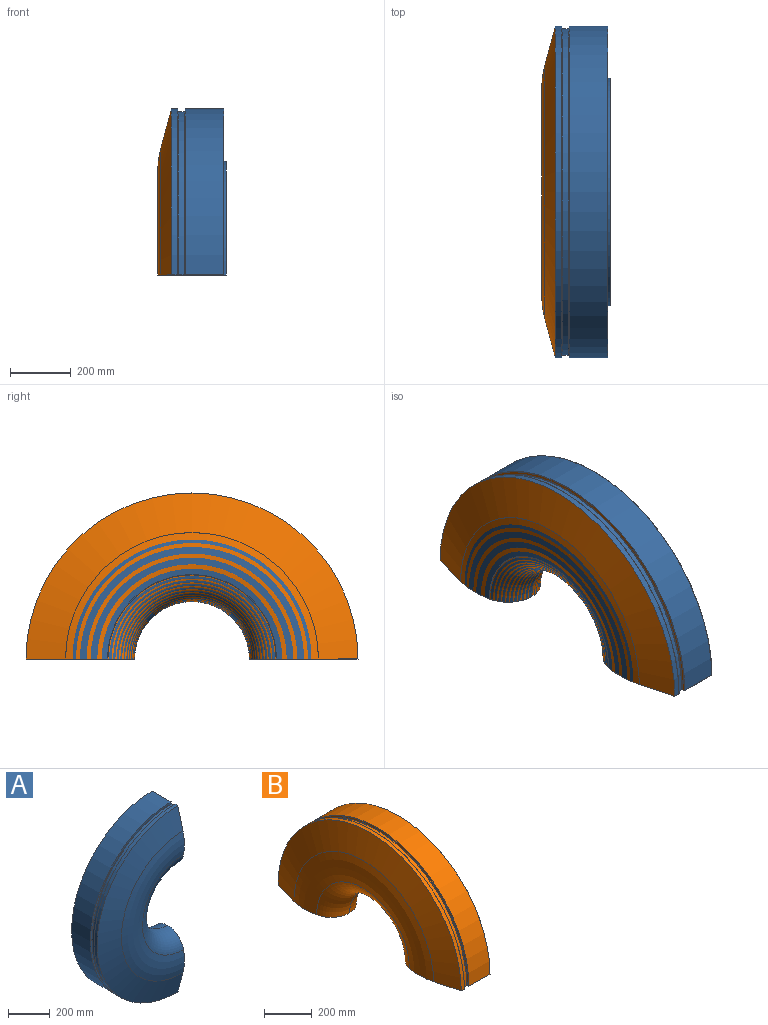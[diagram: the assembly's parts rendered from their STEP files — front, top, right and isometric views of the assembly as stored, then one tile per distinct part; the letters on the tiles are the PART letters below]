
ASSEMBLY  parts=2 mates=1
PART A: 24 faces, bbox 595.3x225x1190.6 mm
  f0: plane 356.3x225mm, normal (1,0,0), area 68121mm2, adj f1,f2,f3,f4,f5,f6,f7,f8
  f1: cone r=414.61mm half-angle=75deg, axis (0,1,0), area 202583mm2, adj f0,f2,f22,f23
  f2: cylinder r=544.5mm len=1089mm, axis (0,-1,0), area 34211.9mm2, adj f0,f1,f3,f23
  f3: plane 1089x544.5mm, normal (0,1,0), area 16948.9mm2, adj f0,f2,f4,f23
  f4: torus R=534.5mm, axis (0,-1,0), area 2634.5mm2, adj f0,f3,f5,f23
  f5: cylinder r=533.5mm len=1067mm, axis (0,-1,0), area 838mm2, adj f0,f4,f6,f23
  f6: cone r=533.5mm half-angle=45deg, axis (0,1,0), area 3560.4mm2, adj f0,f5,f7,f23
  f7: cylinder r=535mm len=1070mm, axis (0,-1,0), area 31934.3mm2, adj f0,f6,f8,f23
  f8: cone r=535mm half-angle=45deg, axis (0,-1,0), area 3560.4mm2, adj f0,f7,f9,f23
  f9: cylinder r=533.5mm len=1067mm, axis (0,-1,0), area 838mm2, adj f0,f8,f10,f23
  f10: torus R=534.5mm, axis (0,-1,0), area 2634.5mm2, adj f0,f9,f11,f23
  f11: plane 1089x544.5mm, normal (0,-1,0), area 16948.9mm2, adj f0,f10,f12,f23
  f12: cylinder r=544.5mm len=1089mm, axis (0,-1,0), area 217245.8mm2, adj f0,f11,f13,f23
  f13: plane 1089x544.5mm, normal (0,1,0), area 235892.8mm2, adj f0,f12,f14,f23
  f14: torus R=381.5mm, axis (0,-1,0), area 1885.8mm2, adj f0,f13,f15,f23
  f15: plane 763x381.5mm, normal (0,1,0), area 9487.6mm2, adj f0,f14,f16,f23
  f16: torus R=373.5mm, axis (0,-1,0), area 1840mm2, adj f0,f15,f17,f23
  f17: cylinder r=372.5mm len=745mm, axis (0,-1,0), area 9361.9mm2, adj f0,f16,f18,f23
  f18: plane 745x372.5mm, normal (0,1,0), area 41217.7mm2, adj f0,f17,f19,f23
  f19: torus R=404.55mm, axis (0,-1,0), area 72929.8mm2, adj f0,f18,f20,f23
  f20: torus R=286.2mm, axis (0,-1,0), area 84815.3mm2, adj f0,f19,f21,f23
  f21: torus R=298.2mm, axis (0,-1,0), area 104462.4mm2, adj f0,f20,f22,f23
  f22: torus R=337mm, axis (0,-1,0), area 151103.6mm2, adj f0,f1,f21,f23
  f23: plane 356.3x225mm, normal (1,0,0), area 68121mm2, adj f1,f2,f3,f4,f5,f6,f7,f8
PART B: 24 faces, bbox 225x1191.2x595.6 mm
  f0: plane 763x381.5mm, normal (1,0,0), area 9487.6mm2, adj f17,f18,f19,f20
  f1: plane 1087x543.5mm, normal (1,0,0), area 234183.7mm2, adj f17,f18,f19,f21
  f2: cylinder r=544.5mm len=1089mm, axis (-1,0,0), area 213824.6mm2, adj f17,f18,f21,f22
  f3: plane 1087x543.5mm, normal (-1,0,0), area 14399.9mm2, adj f4,f17,f18,f22
  f4: torus R=535mm, axis (-1,0,0), area 7906.2mm2, adj f3,f5,f17,f18
  f5: cylinder r=535mm len=1070mm, axis (-1,0,0), area 31934.3mm2, adj f4,f6,f17,f18
  f6: torus R=535mm, axis (-1,0,0), area 7906.2mm2, adj f5,f7,f17,f18
  f7: plane 1087x543.5mm, normal (1,0,0), area 14399.9mm2, adj f6,f17,f18,f23
  f8: cylinder r=544.5mm len=1089mm, axis (-1,0,0), area 32501.3mm2, adj f9,f17,f18,f23
  f9: cone r=544.5mm half-angle=75deg, axis (1,0,0), area 202400.5mm2, adj f8,f10,f17,f18
  f10: torus R=337.02mm, axis (-1,0,0), area 152258.5mm2, adj f9,f11,f17,f18
  f11: torus R=298.2mm, axis (-1,0,0), area 103493.3mm2, adj f10,f12,f17,f18
  f12: torus R=286.2mm, axis (-1,0,0), area 83272.7mm2, adj f11,f13,f17,f18
  f13: torus R=404.4mm, axis (-1,0,0), area 72247.6mm2, adj f12,f14,f17,f18
  f14: torus R=337.6mm, axis (-1,0,0), area 4509mm2, adj f13,f15,f17,f18
  f15: plane 745x372.5mm, normal (1,0,0), area 38925.8mm2, adj f14,f16,f17,f18
  f16: cylinder r=372.5mm len=745mm, axis (-1,0,0), area 9361.9mm2, adj f15,f17,f18,f20
  f17: plane 356.3x225mm, normal (0,0,-1), area 68120.5mm2, adj f0,f1,f2,f3,f4,f5,f6,f7
  f18: plane 356.3x225mm, normal (0,0,-1), area 68120.5mm2, adj f0,f1,f2,f3,f4,f5,f6,f7
  f19: torus R=381.5mm, axis (1,0,0), area 1885.8mm2, adj f0,f1,f17,f18
  f20: torus R=373.5mm, axis (1,0,0), area 1840mm2, adj f0,f16,f17,f18
  f21: cone r=544.5mm half-angle=45deg, axis (-1,0,0), area 2416.9mm2, adj f1,f2,f17,f18
  f22: cone r=543.5mm half-angle=45deg, axis (1,0,0), area 2416.9mm2, adj f2,f3,f17,f18
  f23: cone r=544.5mm half-angle=45deg, axis (-1,0,0), area 2416.9mm2, adj f7,f8,f17,f18
PLACE A rot(axis=(0.58,0.58,-0.58),120deg) t=(-51.37,0,0)mm
PLACE B at identity
MATE revolute A.f1 <-> B.f2  axis (-1,0,0) through (63.5,0,0)mm
